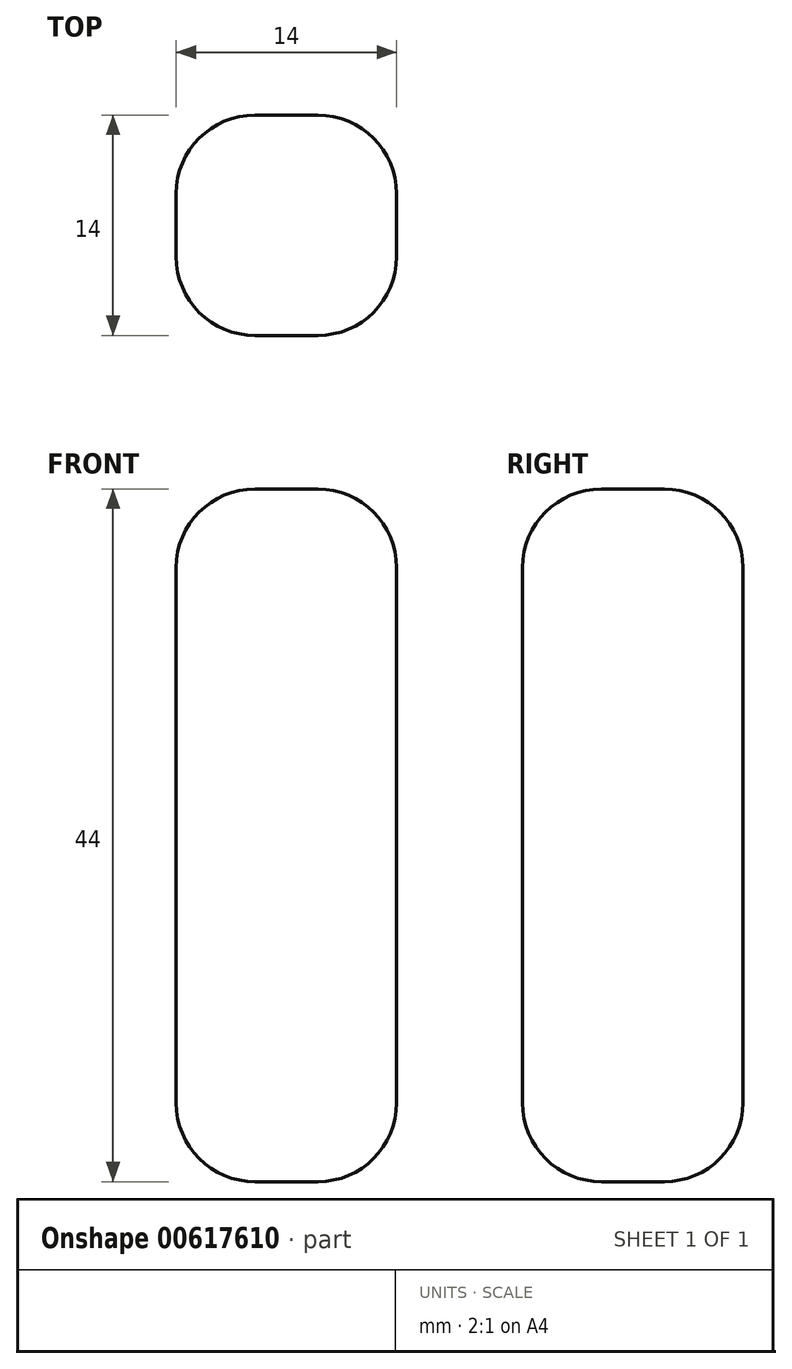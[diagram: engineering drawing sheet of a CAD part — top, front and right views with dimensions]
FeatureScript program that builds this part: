
annotation { "Feature Type Name" : "Feature", "Feature Type Description" : "" }
export const myFeature = defineFeature(function(context is Context, id is Id, definition is map)
    precondition{}
    {
        {
            var Q0;
            Q0=qCreatedBy(makeId("Top.planeOp"),FACE);
            var sketch = newSketch(context, id + "F0", { "sketchPlane" : qUnion([Q0])});
            skLineSegment(sketch, "E0.bottom", {"start": v(7, 7) * mm, "end": v(-7, 7) * mm});
            skLineSegment(sketch, "E0.top", {"start": v(7, -7) * mm, "end": v(-7, -7) * mm});
            skLineSegment(sketch, "E0.left", {"start": v(7, 7) * mm, "end": v(7, -7) * mm});
            skLineSegment(sketch, "E0.right", {"start": v(-7, 7) * mm, "end": v(-7, -7) * mm});
            skPoint(sketch, "E0.middle", {"position": v(0, 0) * mm});
            skSolve(sketch);
        }
        {
            var Q0;
            Q0=makeQuery(id+"F0.imprint","IMPRINT",FACE,{"disambiguationData":[TD([[makeQuery(id+"F0.imprint","IMPRINT",EDGE,{"derivedFrom":sQuery(id+"F0.wireOp",EDGE,"E0.bottom")}),1.0]])]});
            extrude(context, id + "F1", {"entities" : qUnion([Q0]), "depth" : 44 * mm, "offsetDistance" : 25 * mm});
        }
        {
            var Q0;
            Q0=makeQuery(id+"F1.opExtrude","CAP_EDGE",EDGE,{"disambiguationData":[OSD([sQuery(id+"F0.wireOp",EDGE,"E0.top")])],"isStart":true});
            var Q1;
            Q1=makeQuery(id+"F1.opExtrude","CAP_EDGE",EDGE,{"disambiguationData":[OSD([sQuery(id+"F0.wireOp",EDGE,"E0.bottom")])],"isStart":true});
            var Q2;
            Q2=makeQuery(id+"F1.opExtrude","CAP_EDGE",EDGE,{"disambiguationData":[OSD([sQuery(id+"F0.wireOp",EDGE,"E0.top")])],"isStart":false});
            var Q3;
            Q3=makeQuery(id+"F1.opExtrude","CAP_EDGE",EDGE,{"disambiguationData":[OSD([sQuery(id+"F0.wireOp",EDGE,"E0.bottom")])],"isStart":false});
            fillet(context, id + "F2", {"entities" : qUnion([Q0, Q1, Q2, Q3]), "radius" : 5 * mm, "tangentPropagation" : true, "allowEdgeOverflow" : false});
        }
        {
            var Q0;
            Q0=makeQuery(id+"F1.opExtrude","SWEPT_FACE",FACE,{"disambiguationData":[OSD([sQuery(id+"F0.wireOp",EDGE,"E0.bottom")])]});
            fillet(context, id + "F3", {"entities" : qUnion([Q0]), "radius" : 5 * mm, "tangentPropagation" : true, "allowEdgeOverflow" : false});
        }
    });
